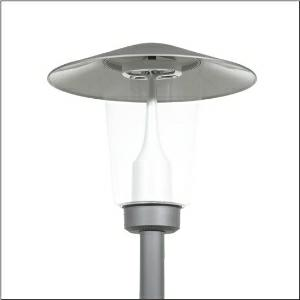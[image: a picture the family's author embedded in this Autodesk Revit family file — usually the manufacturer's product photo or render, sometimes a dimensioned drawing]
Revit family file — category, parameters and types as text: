
# Revit family: pilzleuchte_iq___st1_2a_5xa5235kf14h_dd17
name_source: partatom
category: Lighting Fixtures
units: mm (PartAtom-declared; Revit-internal decimal feet)

## family parameters
Cut with Voids When Loaded = No
Host = Face
Light Source = No
Part Type = Normal
Room Calculation Point = No
Round Connector Dimension = Use Diameter
Shared = No

## types (1)
- --- (1 x LED, 1550 lm, 10 W, 4000K)
    Apparent Load = 10 VA
    CIE Flux Codes = 24 61 93 98 100
    Color Rendering = 70
    Color Temperature = 4000K
    Default Elevation = 1800 mm
    Description = Mushroom Luminaire iQ, mast luminaire, Module 540 iQ-SR, primary light control with 3 zone facetted reflector, of plastic, silver coated, highly specular, structured, primary optical cover: cover, of PMMA, transparent, light distribution: ST1.2a, light emission: direct distribution, primary light characteristic: asymmetric, installation type: post-top, LED, High Power LED, rated luminous flux: 1.550lm, luminous efficacy: 155lm/W, light colour: 740, colour temperature: 4000K, control gear: iQ Street-Remote, control: pre-setting: logarithmic dimming characteristic, Street-Remote, Auto-Match, Temp-Guard, Lumen-Switch, Night-Set, Smart-Wire, Light-Fading, Desk-Remote (wireless, voltage-free reading and setting of iQ features in the workshop via application-optimized NFC function/RFID function), optimised constant luminous flux control (CLO 2.0), with terminal, 6-pole, max. 2.5mm², mains connection: 230..240V, AC, 50/60Hz, start of lifetime: 10W, end of service life: 10W, reduction: 5W, luminaire housing, upper part, of glass-fibre reinforced polyester, coated, Siteco® metallic grey (DB 702S), diameter: 650mm, height: 586mm, spigot size: d x l = 76 x 70mm (post-top) | with reducer (optional accessory) 60 x 70mm, mounting height: 3..5m, post-top mast mounting element, of diecast aluminium, coated, Siteco® metallic grey (DB 702S), Module 540 iQ-SR, traffic white (RAL 9016), equipment: standard, protection rating (complete): IP65, insulation class (complete): insulation class II (safety insulation), certification: CE, ENEC, VDE, packaging unit: 1 piece

Light Distribution: ST1.2a
    Height = 586 mm
    Lamp = 1 x LED
    Lamp Light Flux = 1550 lm
    Lamp Power = 10 W
    Lamp count = 1
    Length = 650 mm
    Luminous efficacy = 155 lm/W
    Manufacturer = Siteco
    ModVariant = No
    Model = 5XA5235KF14H
    Number of Poles = 1
    OnlyDefault = Yes
    Power Factor = 1
    Product Name = Pilzleuchte iQ | ST1.2a
    Product group = mast luminaire | pylon top
    ProductGroupID = 6100
    Protection Class = Protection class II
    Protection Degree = IP 65
    RLX_Detail_Level = 1
    RLX_Emergency_Light_Flux = 0 lm
    RLX_Emergency_Type = 0
    RLX_Emergency_Type_DB = No
    RlxData = <blob elided: 127005 chars, md5=b2fefbc8>
    Socket = socket
    Standby Power = 0 W
    System Light Flux = 1550 lm
    System Power = 10 W
    Type Comments = factory setting: luminous flux: 100 % | dim-lin: 254 | 401 mA
    Type Image = l_1006077.jpg
    URL = http://relux.com
    VarID = @adj_160758
    Voltage = 0 V
    Weight = 0.00 kg
    Width = 0 mm  [stored 0 ft]

note: [stored X ft] marks values corroborated as IEEE doubles in the binary element streams (Revit-internal decimal feet)

## geometry (parser evidence)
native form markers: Blend x4, Sweep x12
no freeform markers — native parametric forms only
